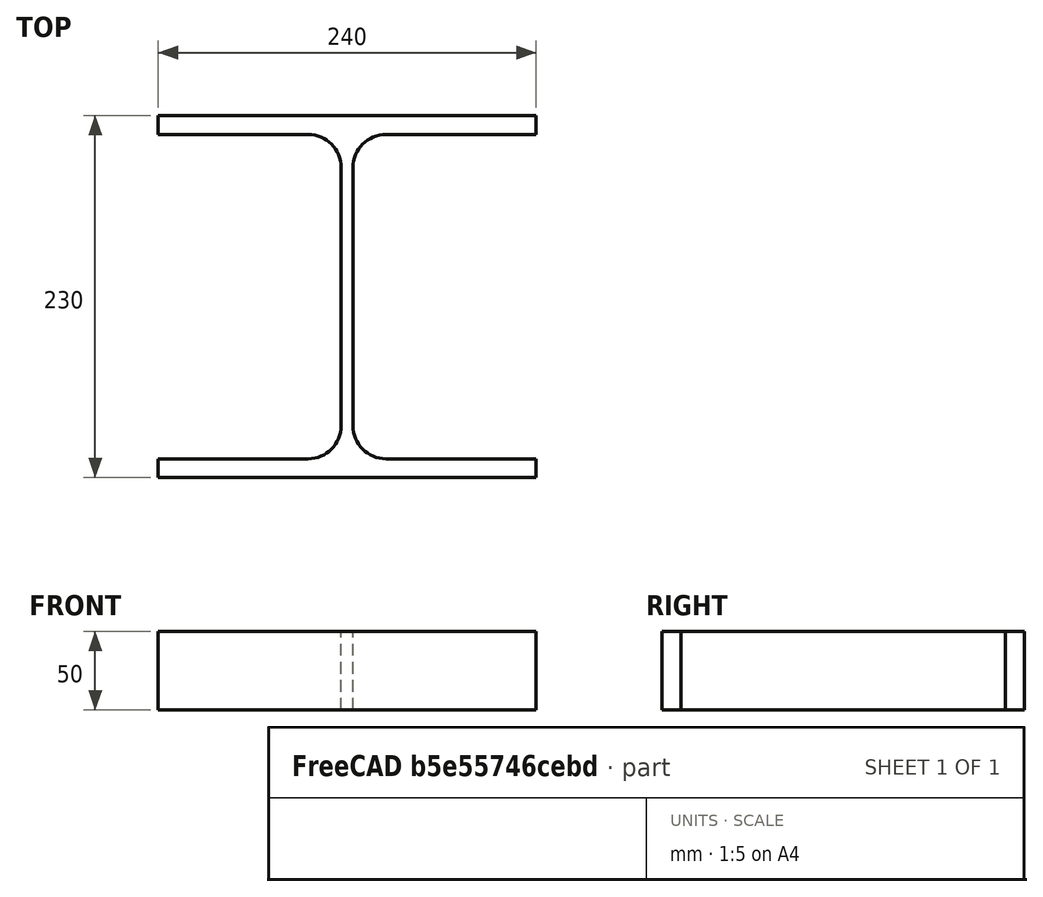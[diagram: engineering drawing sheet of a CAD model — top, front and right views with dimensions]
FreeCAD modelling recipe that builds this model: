
FCSTD DOCUMENT  (FreeCAD 0.15R4671 (Git))
Label: HE-A-Profile 240 DIN1025-3 S235JR
License: All rights reserved
LicenseURL: http://en.wikipedia.org/wiki/All_rights_reserved
objects: Sketcher::SketchObject×1, Part::Extrusion×1
note: 2 computed .brp shape members not serialized (recipe doc carries the construction recipe); baked Part::Feature solids carry a one-line shape summary decoded from their .brp

FEATURE [Sketcher::SketchObject] Sketch
  sketch-geometry (16):
    g0: LineSegment StartX=3.75 StartY=-82 StartZ=0 EndX=3.75 EndY=82 EndZ=0
    g1: LineSegment StartX=24.75 StartY=103 StartZ=0 EndX=120 EndY=103 EndZ=0
    g2: LineSegment StartX=120 StartY=103 StartZ=0 EndX=120 EndY=115 EndZ=0
    g3: LineSegment StartX=120 StartY=115 StartZ=0 EndX=-120 EndY=115 EndZ=0
    g4: LineSegment StartX=-120 StartY=115 StartZ=0 EndX=-120 EndY=103 EndZ=0
    g5: LineSegment StartX=-120 StartY=103 StartZ=0 EndX=-24.75 EndY=103 EndZ=0
    g6: LineSegment StartX=-3.75 StartY=82 StartZ=0 EndX=-3.75 EndY=-82 EndZ=0
    g7: LineSegment StartX=-24.75 StartY=-103 StartZ=0 EndX=-120 EndY=-103 EndZ=0
    g8: LineSegment StartX=-120 StartY=-103 StartZ=0 EndX=-120 EndY=-115 EndZ=0
    g9: LineSegment StartX=-120 StartY=-115 StartZ=0 EndX=120 EndY=-115 EndZ=0
    g10: LineSegment StartX=120 StartY=-115 StartZ=0 EndX=120 EndY=-103 EndZ=0
    g11: LineSegment StartX=120 StartY=-103 StartZ=0 EndX=24.75 EndY=-103 EndZ=0
    g12: ArcOfCircle CenterX=24.75 CenterY=82 CenterZ=0 NormalX=0 NormalY=0 NormalZ=1 Radius=21 StartAngle=1.5708 EndAngle=3.14159
    g13: ArcOfCircle CenterX=24.75 CenterY=-82 CenterZ=0 NormalX=0 NormalY=0 NormalZ=1 Radius=21 StartAngle=3.14159 EndAngle=4.71239
    g14: ArcOfCircle CenterX=-24.75 CenterY=82 CenterZ=0 NormalX=0 NormalY=0 NormalZ=1 Radius=21 StartAngle=0 EndAngle=1.5708
    g15: ArcOfCircle CenterX=-24.75 CenterY=-82 CenterZ=0 NormalX=0 NormalY=0 NormalZ=1 Radius=21 StartAngle=4.71239 EndAngle=6.28319
  constraints (42):
    c: Vertical(g0)
    c: Coincident(g2,g1)
    c: Vertical(g2)
    c: Coincident(g3,g2)
    c: Coincident(g4,g3)
    c: Vertical(g4)
    c: Coincident(g5,g4)
    c: Horizontal(g5)
    c: Vertical(g6)
    c: Horizontal(g7)
    c: Coincident(g8,g7)
    c: Vertical(g8)
    c: Coincident(g9,g8)
    c: Horizontal(g9)
    c: Coincident(g10,g9)
    c: Vertical(g10)
    c: Coincident(g11,g10)
    c: Horizontal(g11)
    c: Tangent(g1,g12) = 1.5708
    c: Tangent(g0,g12) = 1.5708
    c: Tangent(g0,g13) = 1.5708
    c: Tangent(g11,g13) = 1.5708
    c: Tangent(g5,g14) = 1.5708
    c: Tangent(g6,g14) = 1.5708
    c: Tangent(g6,g15) = 1.5708
    c: Tangent(g7,g15) = 1.5708
    c: Equal(g3,g9)
    c: Equal(g2,g4)
    c: Equal(g12,g14)
    c: Equal(g14,g15)
    c: Equal(g15,g13)
    c: Symmetric(g2,g3,g-2)
    c: Symmetric(g9,g8,g-2)
    c: Symmetric(g0,g6,g-2)
    c: Symmetric(g2,g9,g-1)
    c: DistanceY(g2,g9) = -230
    c: DistanceX(g3) = -240
    c: DistanceX(g0,g6) = -7.5
    c: DistanceY(g2) = 12
    c: Radius(g12) = 21
    c: Equal(g8,g10)
    c: Equal(g10,g2)
FEATURE [Part::Extrusion] Extrude  label="HE-A-Profile 240 DIN1025-3 S235JR"
  Base = -> Sketch
  Dir = (0,0,50)
  Solid = true
